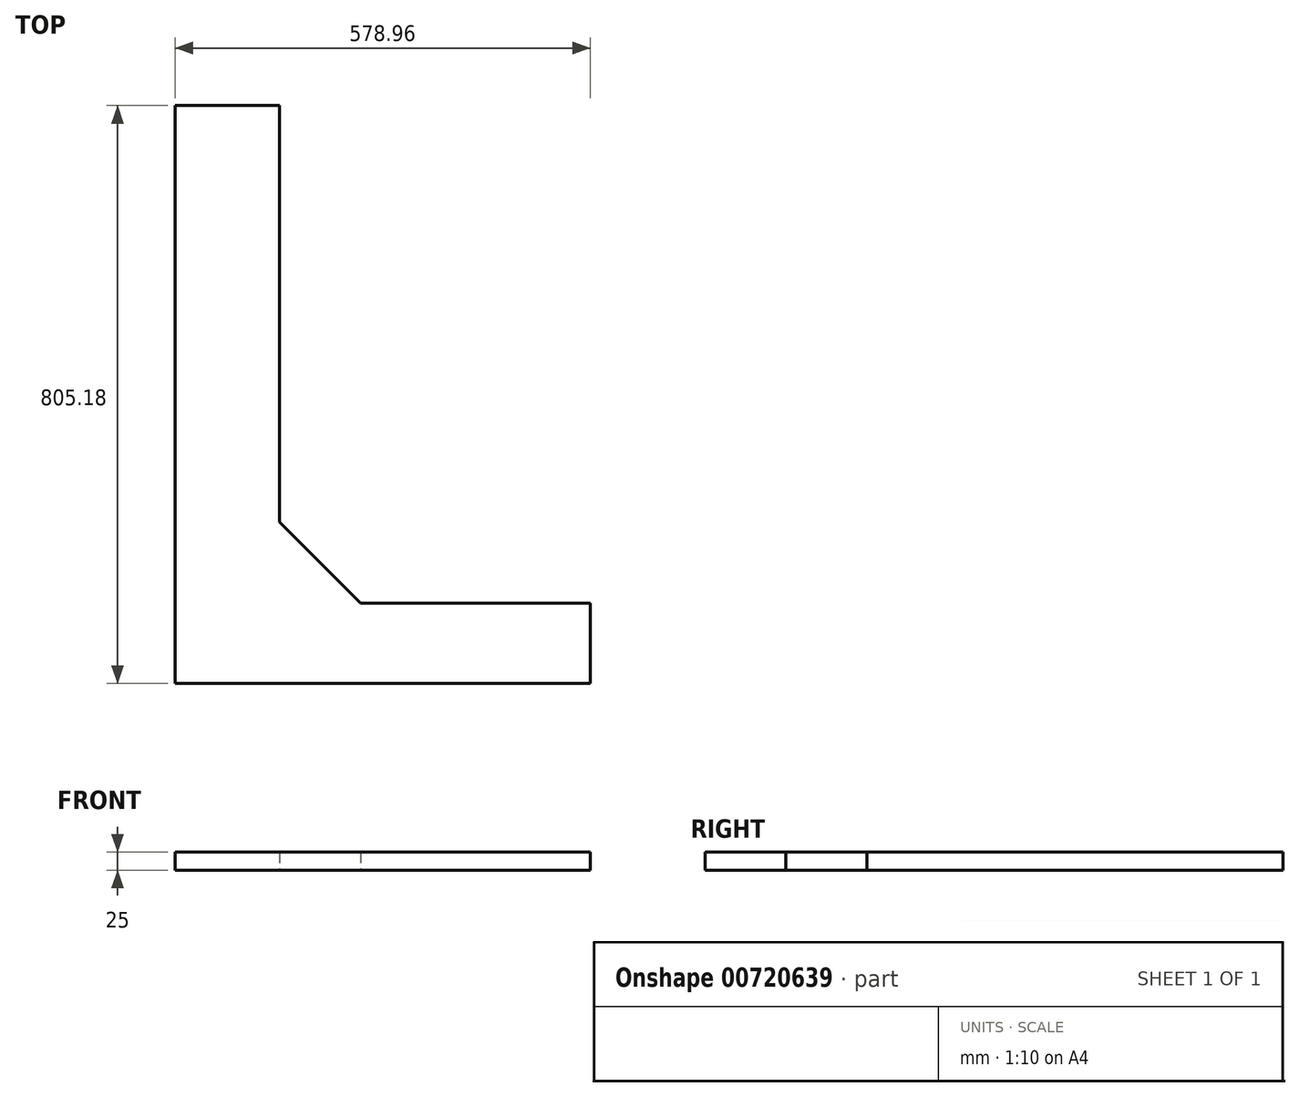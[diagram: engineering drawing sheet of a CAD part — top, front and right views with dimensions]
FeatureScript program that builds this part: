
annotation { "Feature Type Name" : "Feature", "Feature Type Description" : "" }
export const myFeature = defineFeature(function(context is Context, id is Id, definition is map)
    precondition{}
    {
        {
            var Q0;
            Q0=qCreatedBy(makeId("Top.planeOp"),FACE);
            var sketch = newSketch(context, id + "F0", { "sketchPlane" : qUnion([Q0])});
            skLineSegment(sketch, "E0", {"start": v(-371.27, 356.47) * mm, "end": v(-371.27, -223.53) * mm});
            skLineSegment(sketch, "E1", {"start": v(-371.27, -223.53) * mm, "end": v(-258.13, -336.66) * mm});
            skLineSegment(sketch, "E2", {"start": v(-258.13, -336.66) * mm, "end": v(61.87, -336.66) * mm});
            skLineSegment(sketch, "E3", {"start": v(-371.27, 356.47) * mm, "end": v(-517.1, 356.47) * mm});
            skLineSegment(sketch, "E4", {"start": v(-517.1, 356.47) * mm, "end": v(-517.1, -448.71) * mm});
            skLineSegment(sketch, "E5", {"start": v(-517.1, -448.71) * mm, "end": v(61.87, -448.71) * mm});
            skLineSegment(sketch, "E6", {"start": v(61.87, -448.71) * mm, "end": v(61.87, -336.66) * mm});
            skSolve(sketch);
        }
        {
            var Q0;
            Q0 = qSketchRegion(id + "F0", true);
            extrude(context, id + "F1", {"entities" : qUnion([Q0]), "depth" : 25 * mm, "offsetDistance" : 25 * mm});
        }
    });
